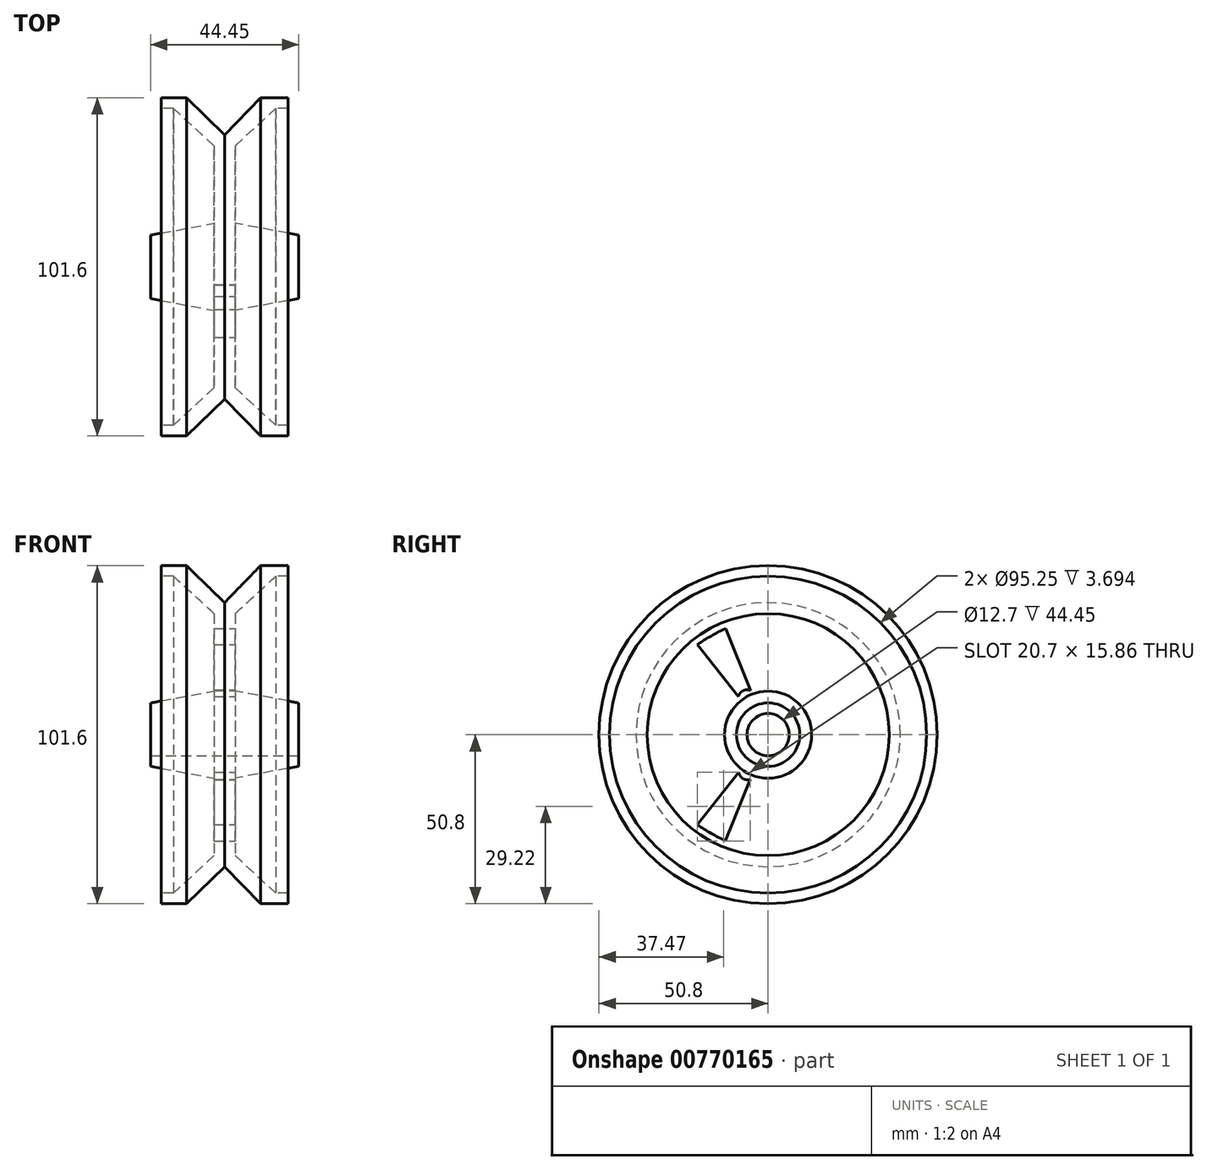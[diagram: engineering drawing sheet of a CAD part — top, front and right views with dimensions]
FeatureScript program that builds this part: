
annotation { "Feature Type Name" : "Feature", "Feature Type Description" : "" }
export const myFeature = defineFeature(function(context is Context, id is Id, definition is map)
    precondition{}
    {
        {
            var Q0;
            Q0=qCreatedBy(makeId("Top.planeOp"),FACE);
            var sketch = newSketch(context, id + "F0", { "sketchPlane" : qUnion([Q0])});
            skLineSegment(sketch, "E0.bottom", {"start": v(0, 0) * mm, "end": v(44.45, 0) * mm});
            skLineSegment(sketch, "E0.top", {"start": v(3.17, 50.8) * mm, "end": v(10.78, 50.8) * mm});
            skLineSegment(sketch, "E0.left", {"start": v(0, 0) * mm, "end": v(0, 9.53) * mm});
            skLineSegment(sketch, "E0.right", {"start": v(44.45, 0) * mm, "end": v(44.45, 9.53) * mm});
            skLineSegment(sketch, "E1", {"start": v(3.17, 50.8) * mm, "end": v(3.17, 47.62) * mm});
            skLineSegment(sketch, "E2", {"start": v(3.17, 47.62) * mm, "end": v(6.87, 47.62) * mm});
            skLineSegment(sketch, "E3", {"start": v(6.87, 47.63) * mm, "end": v(19.05, 36.35) * mm});
            skLineSegment(sketch, "E4", {"start": v(19.05, 36.35) * mm, "end": v(19.05, 13.09) * mm});
            skLineSegment(sketch, "E5", {"start": v(19.05, 13.09) * mm, "end": v(0, 9.53) * mm});
            skLineSegment(sketch, "E6", {"start": v(22.22, 0) * mm, "end": v(22.22, 8.4) * mm});
            skLineSegment(sketch, "E7.MirrorCS", {"start": v(41.28, 50.8) * mm, "end": v(41.28, 47.62) * mm});
            skLineSegment(sketch, "E8.MirrorCS", {"start": v(41.27, 47.62) * mm, "end": v(37.58, 47.62) * mm});
            skLineSegment(sketch, "E9.MirrorCS", {"start": v(37.58, 47.63) * mm, "end": v(25.4, 36.35) * mm});
            skLineSegment(sketch, "E10.MirrorCS", {"start": v(25.4, 36.35) * mm, "end": v(25.4, 13.09) * mm});
            skLineSegment(sketch, "E11.MirrorCS", {"start": v(25.4, 13.09) * mm, "end": v(44.45, 9.53) * mm});
            skLineSegment(sketch, "E12", {"start": v(10.78, 50.8) * mm, "end": v(22.23, 39.7) * mm});
            skLineSegment(sketch, "E13", {"start": v(22.23, 39.7) * mm, "end": v(33, 50.8) * mm});
            skLineSegment(sketch, "E14.trimOffspring", {"start": v(33, 50.8) * mm, "end": v(41.28, 50.8) * mm});
            skSolve(sketch);
        }
        {
            var Q0;
            Q0=makeQuery(id+"F0.imprint","IMPRINT",FACE,{"disambiguationData":[TD([[makeQuery(id+"F0.imprint","IMPRINT",EDGE,{"derivedFrom":sQuery(id+"F0.wireOp",EDGE,"E0.top")}),-1.0]])]});
            var Q1;
            Q1=sQuery(id+"F0.wireOp",EDGE,"E0.bottom");
            revolve(context, id + "F1", {"surfaceOperationType" : NewSurfaceOperationType.NEW, "entities" : qUnion([Q0]), "axis" : qUnion([Q1]), "revolveType" : RevolveType.FULL});
        }
        {
            var Q0;
            Q0=makeQuery(id+"F1.opRevolve","SWEPT_FACE",FACE,{"disambiguationData":[OSD([sQuery(id+"F0.wireOp",EDGE,"E0.right")])]});
            var sketch = newSketch(context, id + "F2", { "sketchPlane" : qUnion([Q0])});
            skCircle(sketch, "E15", {"center": v(0, 0) * mm, "radius": 6.35 * mm});
            skSolve(sketch);
        }
        {
            var Q0;
            Q0=makeQuery(id+"F2.imprint","IMPRINT",FACE,{"disambiguationData":[TD([[makeQuery(id+"F2.imprint","IMPRINT",EDGE,{"derivedFrom":sQuery(id+"F2.wireOp",EDGE,"E15")}),1.0]])]});
            extrude(context, id + "F3", {"entities" : qUnion([Q0]), "operationType" : NewBodyOperationType.REMOVE, "oppositeDirection" : true, "depth" : 76.2 * mm, "offsetDistance" : 25.4 * mm});
        }
        {
            var Q0;
            Q0=makeQuery(id+"F1.opRevolve","SWEPT_FACE",FACE,{"disambiguationData":[OSD([sQuery(id+"F0.wireOp",EDGE,"E7.MirrorCS")])]});
            var sketch = newSketch(context, id + "F4", { "sketchPlane" : qUnion([Q0])});
            skLineSegment(sketch, "E16", {"start": v(14.34, 2.04) * mm, "end": v(34.07, 4.85) * mm});
            skLineSegment(sketch, "E17", {"start": v(34.07, 4.85) * mm, "end": v(14.34, 2.04) * mm});
            skLineSegment(sketch, "E18", {"start": v(14.14, -2.02) * mm, "end": v(34.07, -4.88) * mm});
            skArc(sketch, "E19", {"start": v(34.07, -4.88) * mm, "mid": v(34.24, -0.01) * mm, "end": v(34.07, 4.85) * mm});
            skArc(sketch, "E20", {"start": v(14.14, -2.02) * mm, "mid": v(15.2, -0.04) * mm, "end": v(14.34, 2.04) * mm});
            skLineSegment(sketch, "E21.1.0", {"start": v(-21.24, 27.08) * mm, "end": v(-8.94, 11.4) * mm});
            skArc(sketch, "E21.1.1", {"start": v(-12.8, 31.94) * mm, "mid": v(-17.1, 29.66) * mm, "end": v(-21.24, 27.08) * mm});
            skLineSegment(sketch, "E21.1.2", {"start": v(-5.32, 13.26) * mm, "end": v(-12.8, 31.94) * mm});
            skArc(sketch, "E21.1.3", {"start": v(-5.32, 13.26) * mm, "mid": v(-7.57, 13.19) * mm, "end": v(-8.94, 11.4) * mm});
            skLineSegment(sketch, "E21.2.0", {"start": v(-12.83, -31.93) * mm, "end": v(-5.4, -13.44) * mm});
            skArc(sketch, "E21.2.1", {"start": v(-21.26, -27.06) * mm, "mid": v(-17.13, -29.65) * mm, "end": v(-12.83, -31.93) * mm});
            skLineSegment(sketch, "E21.2.2", {"start": v(-8.82, -11.23) * mm, "end": v(-21.26, -27.06) * mm});
            skArc(sketch, "E21.2.3", {"start": v(-8.82, -11.23) * mm, "mid": v(-7.64, -13.15) * mm, "end": v(-5.4, -13.44) * mm});
            skPoint(sketch, "E21.center", {"position": v(0, 0) * mm});
            skSolve(sketch);
        }
        {
            var Q0;
            Q0=makeQuery(id+"F4.imprint","IMPRINT",FACE,{"disambiguationData":[TD([[makeQuery(id+"F4.imprint","IMPRINT",EDGE,{"derivedFrom":sQuery(id+"F4.wireOp",EDGE,"E21.1.0")}),1.0]])]});
            var Q1;
            Q1=makeQuery(id+"F4.imprint","IMPRINT",FACE,{"disambiguationData":[TD([[makeQuery(id+"F4.imprint","IMPRINT",EDGE,{"derivedFrom":sQuery(id+"F4.wireOp",EDGE,"E17")}),1.0]])]});
            var Q2;
            Q2=makeQuery(id+"F4.imprint","IMPRINT",FACE,{"disambiguationData":[TD([[makeQuery(id+"F4.imprint","IMPRINT",EDGE,{"derivedFrom":sQuery(id+"F4.wireOp",EDGE,"E21.2.0")}),1.0]])]});
            extrude(context, id + "F5", {"entities" : qUnion([Q0, Q1, Q2]), "operationType" : NewBodyOperationType.REMOVE, "endBound" : BoundingType.THROUGH_ALL, "oppositeDirection" : true, "depth" : 25.4 * mm, "offsetDistance" : 25.4 * mm});
        }
    });
